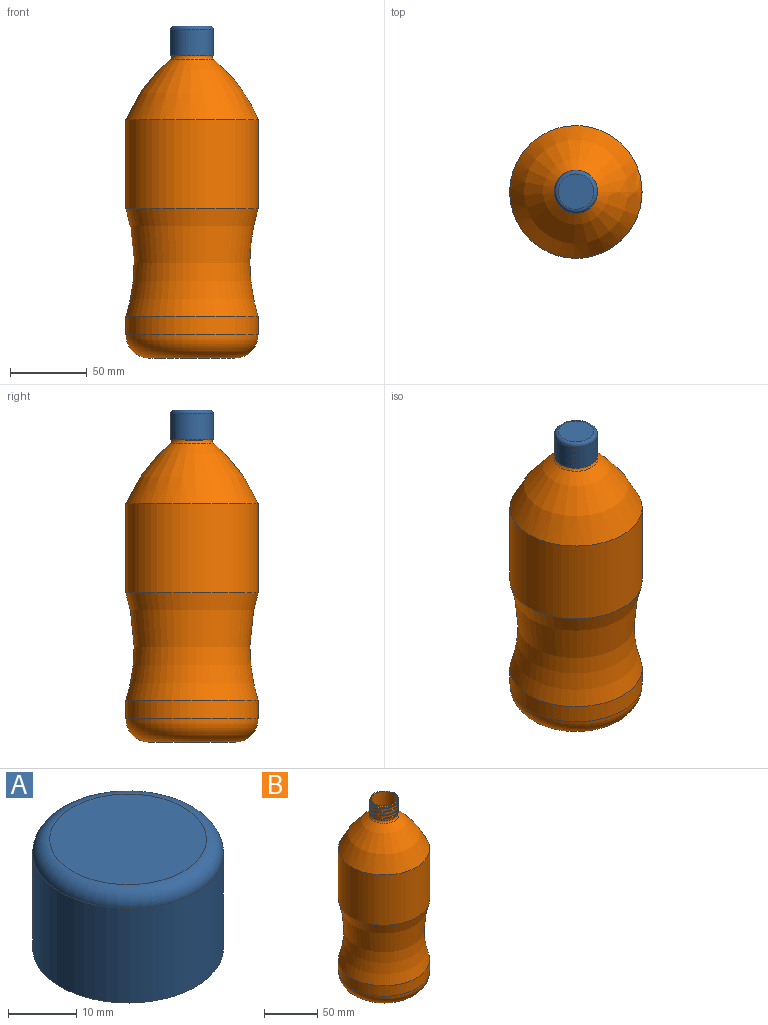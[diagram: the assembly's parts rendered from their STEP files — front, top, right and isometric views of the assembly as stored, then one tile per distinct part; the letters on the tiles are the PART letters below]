
ASSEMBLY  parts=2 mates=1
PART A: 9 faces, bbox 30.4x32.5x20.1 mm
  f0: plane 28x28mm, normal (0,0,-1), area 80mm2, adj f1,f2,f6,f7
  f1: cylinder r=13mm len=26mm, axis (0,0,1), area 788.5mm2, adj f0,f4,f5,f6,f7
  f2: cylinder r=14mm len=28mm, axis (0,0,1), area 1495.4mm2, adj f0,f8
  f3: plane 23x23mm, normal (0,0,1), area 415.5mm2, adj f8
  f4: plane 26x26mm, normal (0,0,-1), area 526.3mm2, adj f1,f5,f7
  f5: plane 0.64x0.64mm, normal (0,1,0.04), area 0.2mm2, adj f1,f4,f7
  f6: plane 1.14x1.14mm, normal (0,-1,-0.04), area 0.6mm2, adj f0,f1,f7
  f7: bspline ~32.33x28.03mm, area 500.4mm2, adj f0,f1,f4,f5,f6
  f8: torus R=11.5mm, axis (0,0,1), area 323mm2, adj f2,f3
PART B: 20 faces, bbox 155.2x155.2x234.8 mm
  f0: torus R=16mm, axis (0,0,1), area 221.1mm2, adj f15,f16,f18,f19
  f1: cylinder r=12mm len=24mm, axis (0,0,1), area 1196mm2, adj f8,f9
  f2: plane 56x56mm, normal (0,0,1), area 2463mm2, adj f3
  f3: torus R=28mm, axis (0,0,1), area 5100.4mm2, adj f2,f4
  f4: cylinder r=42mm len=84mm, axis (0,0,1), area 3126.5mm2, adj f3,f5
  f5: torus R=155.02mm, axis (0,0,1), area 17242.7mm2, adj f4,f6
  f6: cylinder r=42mm len=84mm, axis (0,0,1), area 15214mm2, adj f5,f7
  f7: revolved ~84x84mm, area 8931.9mm2, adj f6,f8
  f8: torus R=16mm, axis (0,0,1), area 278.6mm2, adj f1,f7
  f9: plane 26x26mm, normal (0,0,1), area 74.5mm2, adj f1,f16,f17,f19
  f10: plane 56x56mm, normal (0,0,-1), area 2463mm2, adj f11
  f11: torus R=28mm, axis (0,0,1), area 5559mm2, adj f10,f12
  f12: cylinder r=43mm len=86mm, axis (0,0,1), area 3242.1mm2, adj f11,f13
  f13: torus R=155.02mm, axis (0,0,1), area 17616.9mm2, adj f12,f14
  f14: cylinder r=43mm len=86mm, axis (0,0,1), area 15670.3mm2, adj f13,f15
  f15: revolved ~86x86mm, area 9321.6mm2, adj f0,f14
  f16: cylinder r=13mm len=26mm, axis (0,0,1), area 984.4mm2, adj f0,f9,f17,f18,f19
  f17: plane 1x1mm, normal (0,1,0.05), area 0.6mm2, adj f9,f16,f19
  f18: plane 1x0.5mm, normal (0,-1,-0.05), area 0.4mm2, adj f0,f16,f19
  f19: bspline ~26.98x26.97mm, area 529.8mm2, adj f0,f9,f16,f17,f18
PLACE A rot(axis=(0,0,1),161.5deg) t=(0,0,-3.56)mm
PLACE B at identity fixed
MATE cylindrical A.f1 <-> B.f0  axis (0,0,-1) through (0,0,89.19)mm
